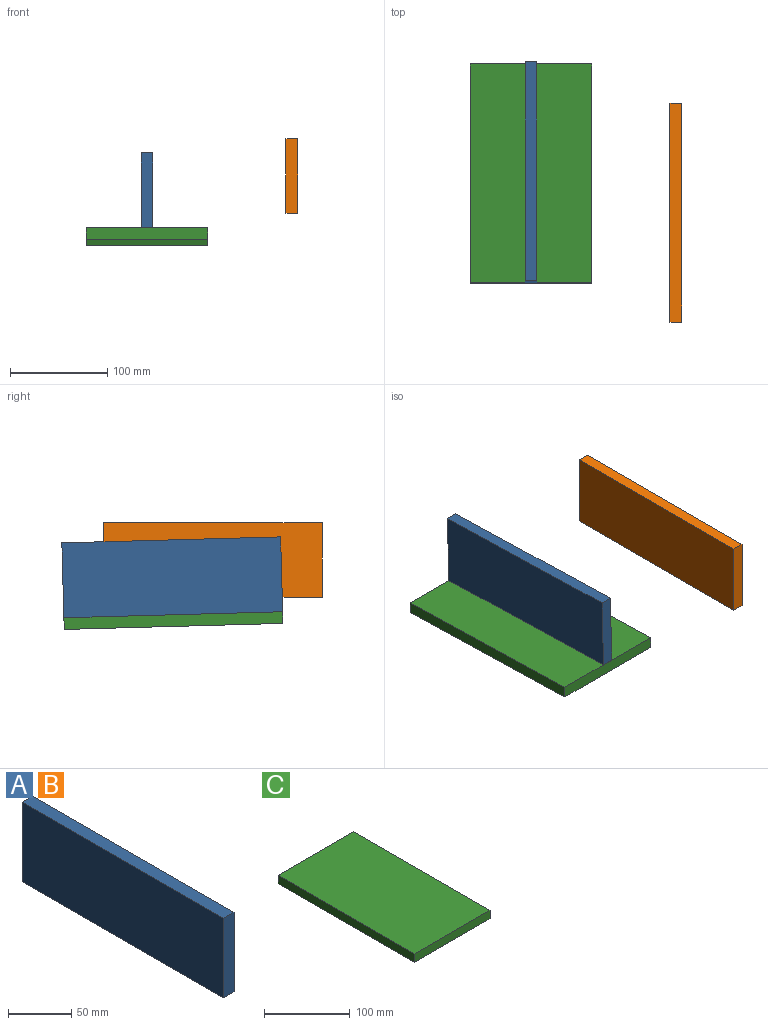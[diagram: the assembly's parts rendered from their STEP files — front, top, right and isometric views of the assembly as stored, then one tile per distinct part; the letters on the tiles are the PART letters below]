
ASSEMBLY  parts=3 mates=1
PART A: 6 faces, bbox 12x225x77 mm
  f0: plane 77x12mm, normal (0,1,0), area 924mm2, adj f1,f3,f4,f5
  f1: plane 225x77mm, normal (-1,0,0), area 17325mm2, adj f0,f2,f4,f5
  f2: plane 77x12mm, normal (0,-1,0), area 924mm2, adj f1,f3,f4,f5
  f3: plane 225x77mm, normal (1,0,0), area 17325mm2, adj f0,f2,f4,f5
  f4: plane 225x12mm, normal (0,0,1), area 2700mm2, adj f0,f1,f2,f3
  f5: plane 225x12mm, normal (0,0,-1), area 2700mm2, adj f0,f1,f2,f3
PART B: same geometry as A
PART C: 6 faces, bbox 125x225x12 mm
  f0: plane 225x12mm, normal (1,0,0), area 2700mm2, adj f1,f3,f4,f5
  f1: plane 125x12mm, normal (0,1,0), area 1500mm2, adj f0,f2,f4,f5
  f2: plane 225x12mm, normal (-1,0,0), area 2700mm2, adj f1,f3,f4,f5
  f3: plane 125x12mm, normal (0,-1,0), area 1500mm2, adj f0,f2,f4,f5
  f4: plane 225x125mm, normal (0,0,1), area 28125mm2, adj f0,f1,f2,f3
  f5: plane 225x125mm, normal (0,0,-1), area 28125mm2, adj f0,f1,f2,f3
PLACE A rot(axis=(-1,0,0),1.6deg) t=(39.23,148.39,-64.31)mm
PLACE B t=(187.99,107.83,-45.49)mm
PLACE C rot(axis=(-1,0,0),1.6deg) t=(-19.04,110.47,-75.27)mm
MATE fastened A.f5 <-> C.f4  axis (0,-0.03,-1) through (-19.04,110.8,-63.28)mm
